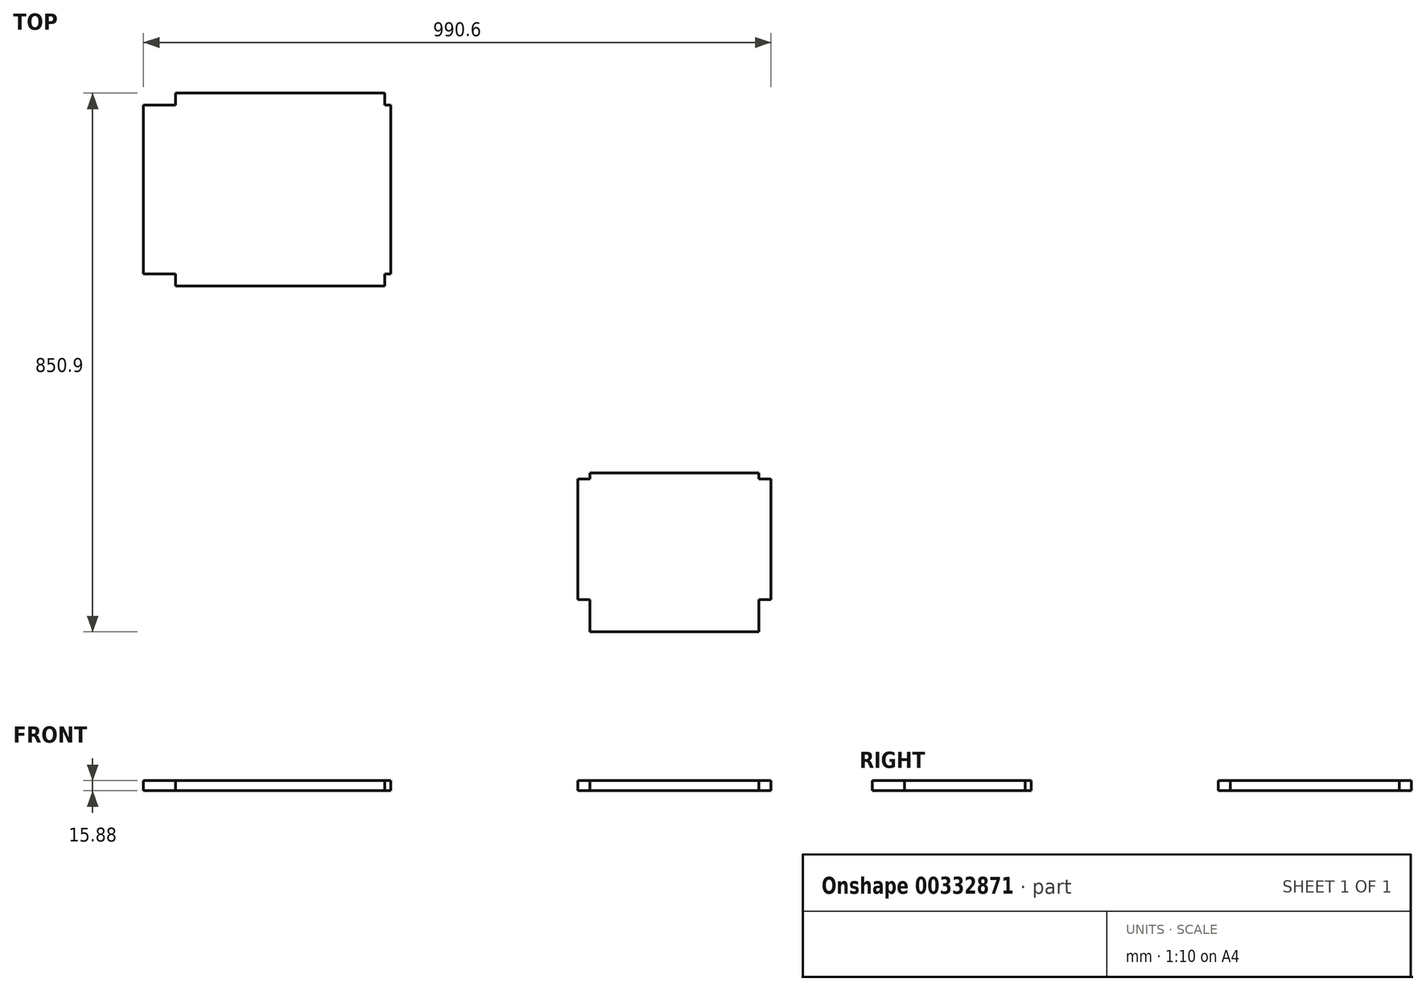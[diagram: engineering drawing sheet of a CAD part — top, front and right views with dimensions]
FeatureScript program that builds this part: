
annotation { "Feature Type Name" : "Feature", "Feature Type Description" : "" }
export const myFeature = defineFeature(function(context is Context, id is Id, definition is map)
    precondition{}
    {
        {
            var Q0;
            Q0=qCreatedBy(makeId("Top.planeOp"),FACE);
            var sketch = newSketch(context, id + "F0", { "sketchPlane" : qUnion([Q0])});
            skLineSegment(sketch, "E0.bottom", {"start": v(209.55, -425.45) * mm, "end": v(476.25, -425.45) * mm});
            skLineSegment(sketch, "E0.top", {"start": v(-444.5, 425.45) * mm, "end": v(-114.41, 425.45) * mm});
            skLineSegment(sketch, "E0.left", {"start": v(-495.3, 139.7) * mm, "end": v(-495.3, 406.4) * mm});
            skLineSegment(sketch, "E0.right", {"start": v(495.3, -374.65) * mm, "end": v(495.3, -184.26) * mm});
            skPoint(sketch, "E0.middle", {"position": v(0, 0) * mm});
            skLineSegment(sketch, "E1.left", {"start": v(190.5, -374.65) * mm, "end": v(190.5, -184.26) * mm});
            skPoint(sketch, "E2.orphan", {"position": v(-495.3, -425.45) * mm});
            skLineSegment(sketch, "E3", {"start": v(-444.5, 120.65) * mm, "end": v(-114.41, 120.65) * mm});
            skLineSegment(sketch, "E4.top", {"start": v(-495.3, 139.7) * mm, "end": v(-444.5, 139.7) * mm});
            skLineSegment(sketch, "E4.right", {"start": v(-444.5, 120.65) * mm, "end": v(-444.5, 139.7) * mm});
            skLineSegment(sketch, "E5.top", {"start": v(-495.3, 406.4) * mm, "end": v(-444.5, 406.4) * mm});
            skLineSegment(sketch, "E5.right", {"start": v(-444.5, 425.45) * mm, "end": v(-444.5, 406.4) * mm});
            skLineSegment(sketch, "E6.top", {"start": v(190.5, -374.65) * mm, "end": v(209.55, -374.65) * mm});
            skLineSegment(sketch, "E6.right", {"start": v(209.55, -425.45) * mm, "end": v(209.55, -374.65) * mm});
            skLineSegment(sketch, "E7.top", {"start": v(476.25, -374.65) * mm, "end": v(495.3, -374.65) * mm});
            skLineSegment(sketch, "E7.left", {"start": v(476.25, -425.45) * mm, "end": v(476.25, -374.65) * mm});
            skPoint(sketch, "E8.orphan", {"position": v(-495.3, 425.45) * mm});
            skPoint(sketch, "E9.orphan", {"position": v(495.3, -425.45) * mm});
            skPoint(sketch, "E10.orphan", {"position": v(495.3, 425.45) * mm});
            skLineSegment(sketch, "E11.top", {"start": v(-114.41, 139.7) * mm, "end": v(-104.89, 139.7) * mm});
            skLineSegment(sketch, "E11.left", {"start": v(-114.41, 120.65) * mm, "end": v(-114.41, 139.7) * mm});
            skLineSegment(sketch, "E12.bottom", {"start": v(190.5, -184.26) * mm, "end": v(209.55, -184.26) * mm});
            skLineSegment(sketch, "E12.right", {"start": v(209.55, -184.26) * mm, "end": v(209.55, -174.74) * mm});
            skPoint(sketch, "E13.orphan", {"position": v(190.5, -158.86) * mm});
            skPoint(sketch, "E14.orphan", {"position": v(-89.01, 120.65) * mm});
            skLineSegment(sketch, "E15.bottom", {"start": v(-114.41, 406.4) * mm, "end": v(-104.89, 406.4) * mm});
            skLineSegment(sketch, "E15.left", {"start": v(-114.41, 406.4) * mm, "end": v(-114.41, 425.45) * mm});
            skLineSegment(sketch, "E16.bottom", {"start": v(476.25, -184.26) * mm, "end": v(495.3, -184.26) * mm});
            skLineSegment(sketch, "E16.top", {"start": v(476.25, -133.46) * mm, "end": v(495.3, -133.46) * mm});
            skLineSegment(sketch, "E16.left", {"start": v(476.25, -184.26) * mm, "end": v(476.25, -174.74) * mm});
            skLineSegment(sketch, "E17", {"start": v(-104.89, 406.4) * mm, "end": v(-104.89, 139.7) * mm});
            skLineSegment(sketch, "E18", {"start": v(476.25, -174.74) * mm, "end": v(209.55, -174.74) * mm});
            skPoint(sketch, "E19.end.orphan", {"position": v(-71.05, 102.69) * mm});
            skPoint(sketch, "E20.start.orphan", {"position": v(172.54, -140.9) * mm});
            skSolve(sketch);
        }
        {
            var Q0;
            Q0=qSketchRegion(id+"F0",true);
            extrude(context, id + "F1", {"entities" : qUnion([Q0]), "depth" : 15.88 * mm});
        }
    });
